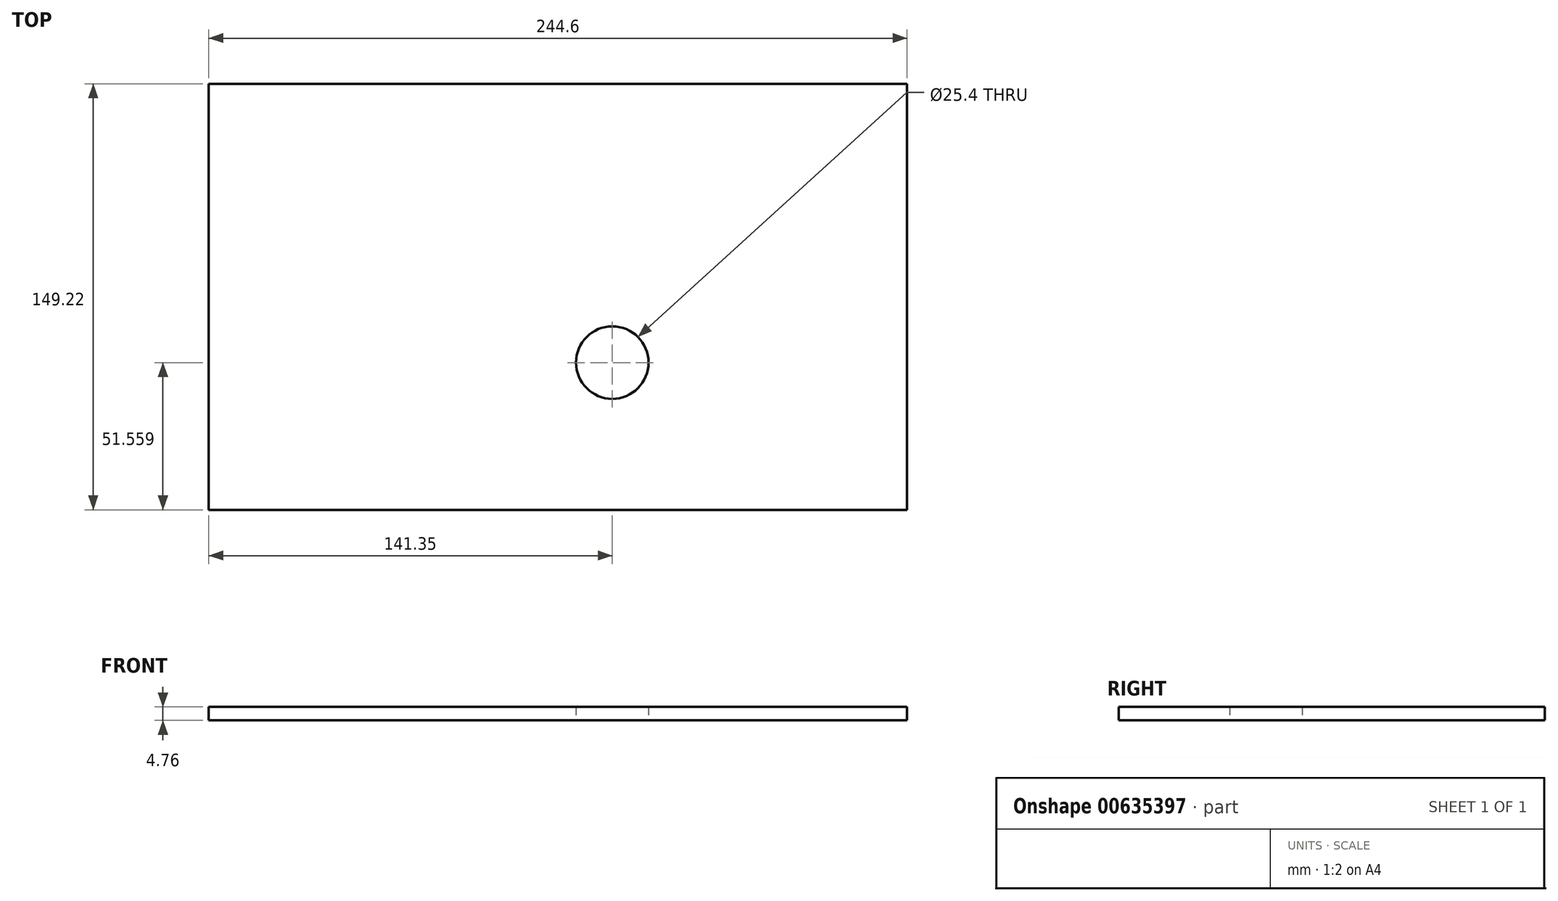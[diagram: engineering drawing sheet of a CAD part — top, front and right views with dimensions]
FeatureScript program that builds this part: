
annotation { "Feature Type Name" : "Feature", "Feature Type Description" : "" }
export const myFeature = defineFeature(function(context is Context, id is Id, definition is map)
    precondition{}
    {
        {
            var Q0;
            Q0=qCreatedBy(makeId("Top.planeOp"),FACE);
            var sketch = newSketch(context, id + "F0", { "sketchPlane" : qUnion([Q0])});
            skLineSegment(sketch, "E0.bottom", {"start": v(-122.3, 74.61) * mm, "end": v(122.3, 74.61) * mm});
            skLineSegment(sketch, "E0.top", {"start": v(-122.3, -74.61) * mm, "end": v(122.3, -74.61) * mm});
            skLineSegment(sketch, "E0.left", {"start": v(-122.3, 74.61) * mm, "end": v(-122.3, -74.61) * mm});
            skLineSegment(sketch, "E0.right", {"start": v(122.3, 74.61) * mm, "end": v(122.3, -74.61) * mm});
            skPoint(sketch, "E0.middle", {"position": v(0, 0) * mm});
            skLineSegment(sketch, "E1", {"start": v(0, 0) * mm, "end": v(0, -74.61) * mm});
            skCircle(sketch, "E2", {"center": v(19.05, -23.05) * mm, "radius": 12.7 * mm});
            skSolve(sketch);
        }
        {
            var Q0;
            Q0=qSketchRegion(id+"F0",true);
            extrude(context, id + "F1", {"entities" : qUnion([Q0]), "depth" : 4.76 * mm});
        }
    });
